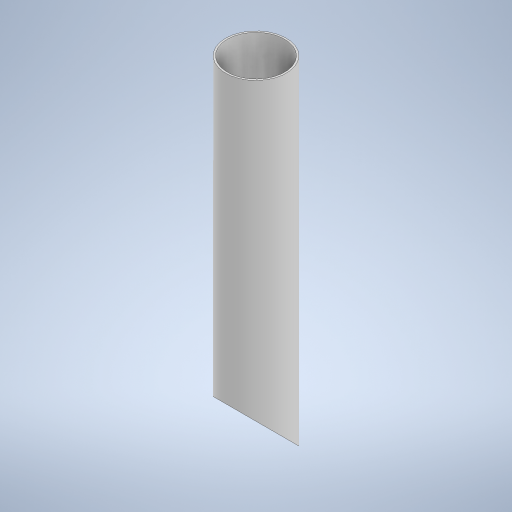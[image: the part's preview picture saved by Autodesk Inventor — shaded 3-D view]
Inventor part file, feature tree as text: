
AUTODESK INVENTOR PART (.ipt)
format: ipt  version: 2024.3 (Build 283343000, 343)  size: 239,104 bytes
history: native  units: mm
features: extrude x2, sketch x2
ambient origin geometry x8: Origin, YZ Plane, XZ Plane, XY Plane, X Axis, Y Axis, Z Axis, Center Point
bodies: Solid1 (feature_tree)
feature tree (4):
  extrude  "Extrusion1"  Depth=70.0mm
  extrude  "Extrusion2"  Depth=400.0mm
  sketch  "Sketch1"  dims[d0=2.0mm d1=70.0mm]
  sketch  "Sketch2"  dims[d2=400.0mm d3=0.0mm d4=70.0mm d5=0.0mm d6=0.0mm]
